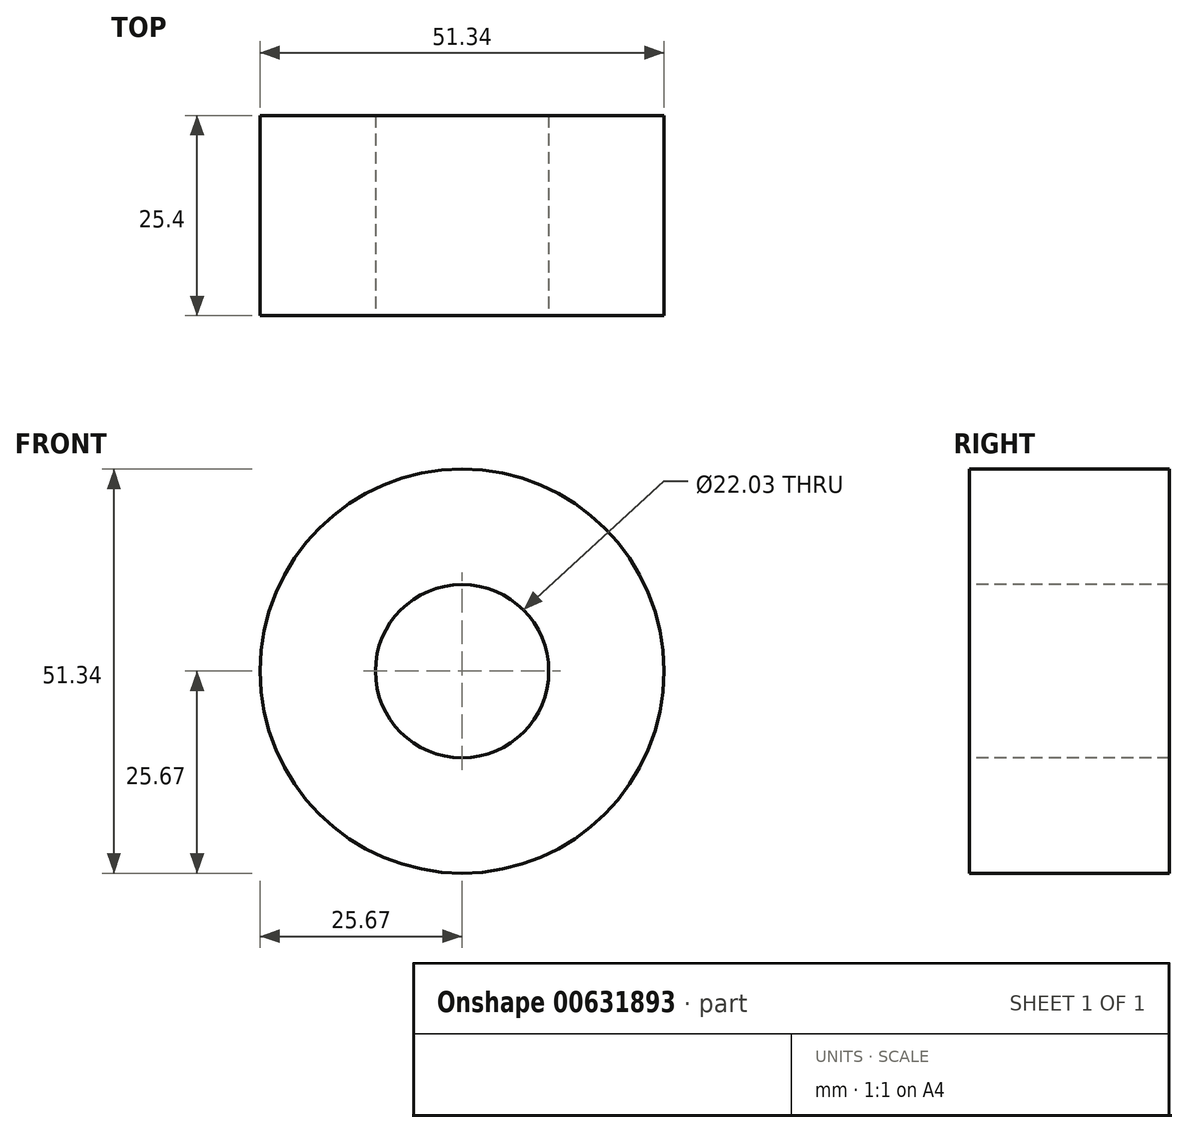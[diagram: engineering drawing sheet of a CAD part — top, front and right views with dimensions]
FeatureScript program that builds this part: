
annotation { "Feature Type Name" : "Feature", "Feature Type Description" : "" }
export const myFeature = defineFeature(function(context is Context, id is Id, definition is map)
    precondition{}
    {
        {
            var Q0;
            Q0=qCreatedBy(makeId("Front.planeOp"),FACE);
            var sketch = newSketch(context, id + "F0", { "sketchPlane" : qUnion([Q0])});
            skCircle(sketch, "E0", {"center": v(0, 0) * mm, "radius": 25.67 * mm});
            skSolve(sketch);
        }
        {
            var Q0;
            Q0=makeQuery(id+"F0.imprint","IMPRINT",FACE,{"disambiguationData":[TD([[makeQuery(id+"F0.imprint","IMPRINT",EDGE,{"derivedFrom":sQuery(id+"F0.wireOp",EDGE,"E0")}),1.0]])]});
            extrude(context, id + "F1", {"entities" : qUnion([Q0]), "depth" : 25.4 * mm, "offsetDistance" : 25.4 * mm});
        }
        {
            var Q0;
            Q0=makeQuery(id+"F1.opExtrude","CAP_FACE",FACE,{"disambiguationData":[OSD([sQuery(id+"F0.wireOp",EDGE,"E0")])],"isStart":false});
            var sketch = newSketch(context, id + "F2", { "sketchPlane" : qUnion([Q0])});
            skCircle(sketch, "E1", {"center": v(0, 0) * mm, "radius": 11.01 * mm});
            skSolve(sketch);
        }
        {
            var Q0;
            Q0=makeQuery(id+"F2.imprint","IMPRINT",FACE,{"disambiguationData":[TD([[makeQuery(id+"F2.imprint","IMPRINT",EDGE,{"derivedFrom":sQuery(id+"F2.wireOp",EDGE,"E1")}),1.0]])]});
            extrude(context, id + "F3", {"entities" : qUnion([Q0]), "operationType" : NewBodyOperationType.REMOVE, "endBound" : BoundingType.UP_TO_NEXT, "oppositeDirection" : true, "depth" : 25.4 * mm, "offsetDistance" : 25.4 * mm});
        }
    });
